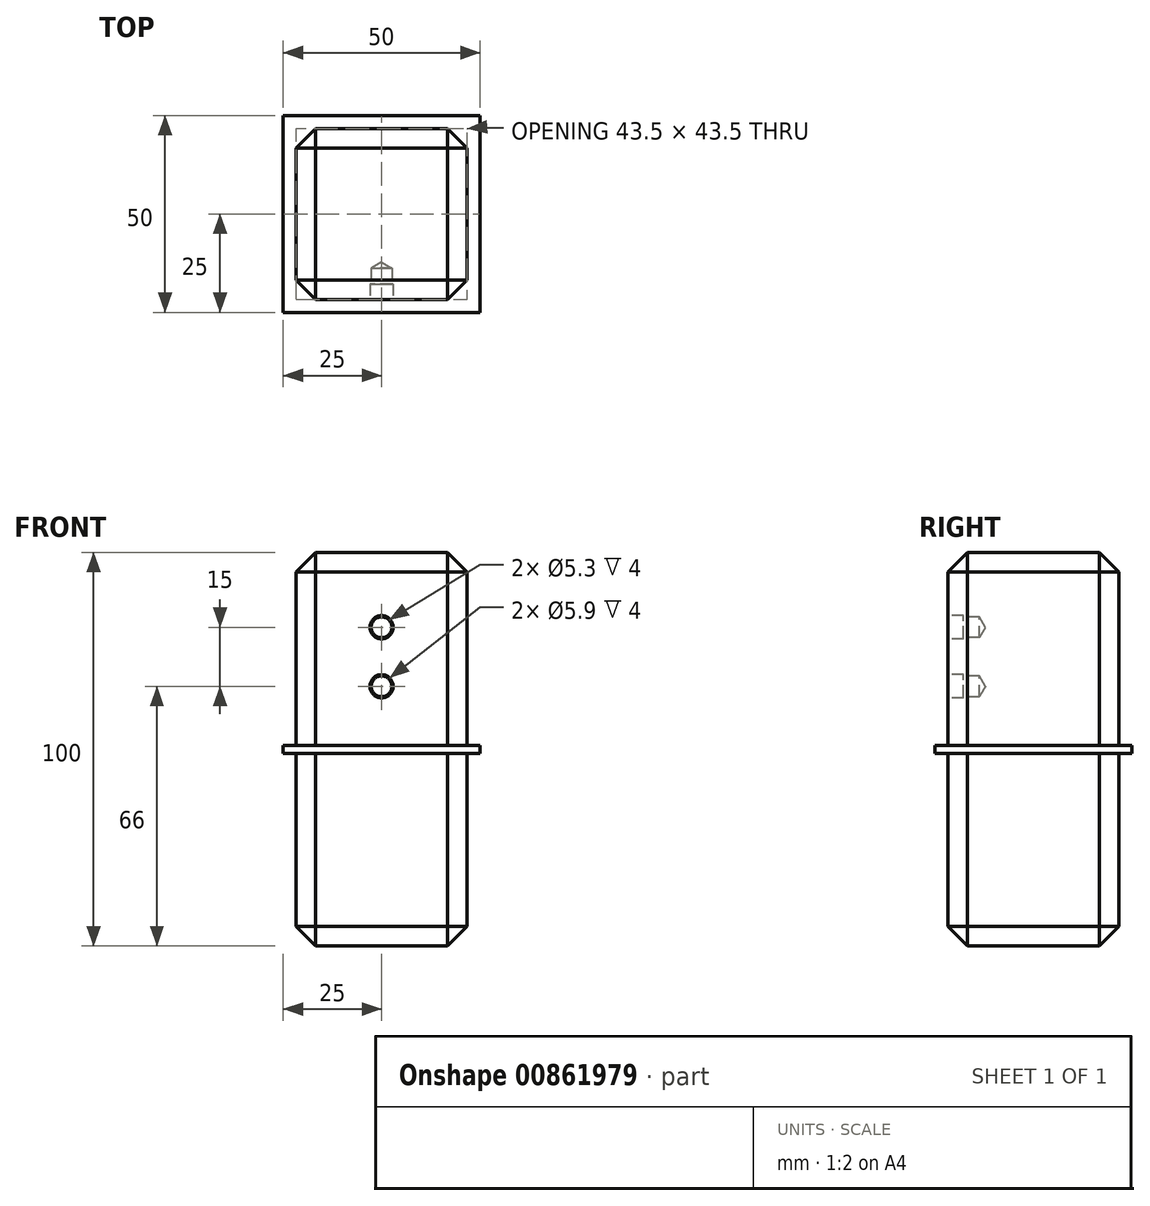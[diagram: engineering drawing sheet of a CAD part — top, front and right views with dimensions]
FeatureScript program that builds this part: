
annotation { "Feature Type Name" : "Feature", "Feature Type Description" : "" }
export const myFeature = defineFeature(function(context is Context, id is Id, definition is map)
    precondition{}
    {
        {
            var Q0;
            Q0=qCreatedBy(makeId("Top.planeOp"),FACE);
            var sketch = newSketch(context, id + "F0", { "sketchPlane" : qUnion([Q0])});
            skLineSegment(sketch, "E0.bottom", {"start": v(-22.5, 22.5) * mm, "end": v(22.5, 22.5) * mm, "construction": true});
            skLineSegment(sketch, "E0.top", {"start": v(-22.5, -22.5) * mm, "end": v(22.5, -22.5) * mm, "construction": true});
            skLineSegment(sketch, "E0.left", {"start": v(-22.5, 22.5) * mm, "end": v(-22.5, -22.5) * mm, "construction": true});
            skLineSegment(sketch, "E0.right", {"start": v(22.5, 22.5) * mm, "end": v(22.5, -22.5) * mm, "construction": true});
            skPoint(sketch, "E0.middle", {"position": v(0, 0) * mm});
            skLineSegment(sketch, "E1.bottom", {"start": v(-21.75, 21.75) * mm, "end": v(21.75, 21.75) * mm});
            skLineSegment(sketch, "E1.top", {"start": v(-21.75, -21.75) * mm, "end": v(21.75, -21.75) * mm});
            skLineSegment(sketch, "E1.left", {"start": v(-21.75, 21.75) * mm, "end": v(-21.75, -21.75) * mm});
            skLineSegment(sketch, "E1.right", {"start": v(21.75, 21.75) * mm, "end": v(21.75, -21.75) * mm});
            skSolve(sketch);
        }
        {
            var Q0;
            Q0 = qSketchRegion(id + "F0", true);
            extrude(context, id + "F1", {"entities" : qUnion([Q0]), "depth" : 100 * mm, "offsetDistance" : 25 * mm, "symmetric" : true});
        }
        {
            var Q0;
            Q0=qCreatedBy(makeId("Top.planeOp"),FACE);
            var sketch = newSketch(context, id + "F2", { "sketchPlane" : qUnion([Q0])});
            skLineSegment(sketch, "E2.bottom", {"start": v(-25, 25) * mm, "end": v(25, 25) * mm});
            skLineSegment(sketch, "E2.top", {"start": v(-25, -25) * mm, "end": v(25, -25) * mm});
            skLineSegment(sketch, "E2.left", {"start": v(-25, 25) * mm, "end": v(-25, -25) * mm});
            skLineSegment(sketch, "E2.right", {"start": v(25, 25) * mm, "end": v(25, -25) * mm});
            skPoint(sketch, "E2.middle", {"position": v(0, 0) * mm});
            skSolve(sketch);
        }
        {
            var Q0;
            Q0 = qSketchRegion(id + "F2", true);
            extrude(context, id + "F3", {"entities" : qUnion([Q0]), "operationType" : NewBodyOperationType.ADD, "depth" : 2 * mm, "offsetDistance" : 25 * mm, "symmetric" : true});
        }
        {
            var Q0;
            Q0=makeQuery(id+"F1.opExtrude","CAP_FACE",FACE,{"disambiguationData":[OSD([sQuery(id+"F0.wireOp",EDGE,"E1.bottom"),sQuery(id+"F0.wireOp",EDGE,"E1.top"),sQuery(id+"F0.wireOp",EDGE,"E1.left"),sQuery(id+"F0.wireOp",EDGE,"E1.right")])],"isStart":false});
            var Q1;
            {var subQ0=sQuery(id+"F0.wireOp",EDGE,"E1.bottom");var subQ1=sQuery(id+"F0.wireOp",EDGE,"E1.left");Q1=makeQuery(id+"F3.boolean.opBoolean","SPLIT",EDGE,{"disambiguationData":[TD([makeQuery(id+"F1.opExtrude","CAP_FACE",FACE,{"disambiguationData":[OSD([subQ0,sQuery(id+"F0.wireOp",EDGE,"E1.top"),subQ1,sQuery(id+"F0.wireOp",EDGE,"E1.right")])],"isStart":false})])],"derivedFrom":makeQuery(id+"F1.opExtrude","SWEPT_EDGE",EDGE,{"disambiguationData":[OSD([subQ0,subQ1])]})});}
            var Q2;
            {var subQ0=sQuery(id+"F0.wireOp",EDGE,"E1.left");var subQ1=sQuery(id+"F0.wireOp",EDGE,"E1.top");Q2=makeQuery(id+"F3.boolean.opBoolean","SPLIT",EDGE,{"disambiguationData":[TD([makeQuery(id+"F1.opExtrude","CAP_FACE",FACE,{"disambiguationData":[OSD([sQuery(id+"F0.wireOp",EDGE,"E1.bottom"),subQ1,subQ0,sQuery(id+"F0.wireOp",EDGE,"E1.right")])],"isStart":false})])],"derivedFrom":makeQuery(id+"F1.opExtrude","SWEPT_EDGE",EDGE,{"disambiguationData":[OSD([subQ1,subQ0])]})});}
            var Q3;
            {var subQ0=sQuery(id+"F0.wireOp",EDGE,"E1.bottom");var subQ1=sQuery(id+"F0.wireOp",EDGE,"E1.right");Q3=makeQuery(id+"F3.boolean.opBoolean","SPLIT",EDGE,{"disambiguationData":[TD([makeQuery(id+"F1.opExtrude","CAP_FACE",FACE,{"disambiguationData":[OSD([subQ0,sQuery(id+"F0.wireOp",EDGE,"E1.top"),sQuery(id+"F0.wireOp",EDGE,"E1.left"),subQ1])],"isStart":false})])],"derivedFrom":makeQuery(id+"F1.opExtrude","SWEPT_EDGE",EDGE,{"disambiguationData":[OSD([subQ0,subQ1])]})});}
            var Q4;
            {var subQ0=sQuery(id+"F0.wireOp",EDGE,"E1.right");var subQ1=sQuery(id+"F0.wireOp",EDGE,"E1.top");Q4=makeQuery(id+"F3.boolean.opBoolean","SPLIT",EDGE,{"disambiguationData":[TD([makeQuery(id+"F1.opExtrude","CAP_FACE",FACE,{"disambiguationData":[OSD([sQuery(id+"F0.wireOp",EDGE,"E1.bottom"),subQ1,sQuery(id+"F0.wireOp",EDGE,"E1.left"),subQ0])],"isStart":false})])],"derivedFrom":makeQuery(id+"F1.opExtrude","SWEPT_EDGE",EDGE,{"disambiguationData":[OSD([subQ1,subQ0])]})});}
            var Q5;
            {var subQ0=sQuery(id+"F0.wireOp",EDGE,"E1.left");var subQ1=sQuery(id+"F0.wireOp",EDGE,"E1.top");Q5=makeQuery(id+"F3.boolean.opBoolean","SPLIT",EDGE,{"disambiguationData":[TD([makeQuery(id+"F1.opExtrude","CAP_FACE",FACE,{"disambiguationData":[OSD([sQuery(id+"F0.wireOp",EDGE,"E1.bottom"),subQ1,subQ0,sQuery(id+"F0.wireOp",EDGE,"E1.right")])],"isStart":true})])],"derivedFrom":makeQuery(id+"F1.opExtrude","SWEPT_EDGE",EDGE,{"disambiguationData":[OSD([subQ1,subQ0])]})});}
            var Q6;
            {var subQ0=sQuery(id+"F0.wireOp",EDGE,"E1.right");var subQ1=sQuery(id+"F0.wireOp",EDGE,"E1.top");Q6=makeQuery(id+"F3.boolean.opBoolean","SPLIT",EDGE,{"disambiguationData":[TD([makeQuery(id+"F1.opExtrude","CAP_FACE",FACE,{"disambiguationData":[OSD([sQuery(id+"F0.wireOp",EDGE,"E1.bottom"),subQ1,sQuery(id+"F0.wireOp",EDGE,"E1.left"),subQ0])],"isStart":true})])],"derivedFrom":makeQuery(id+"F1.opExtrude","SWEPT_EDGE",EDGE,{"disambiguationData":[OSD([subQ1,subQ0])]})});}
            var Q7;
            {var subQ0=sQuery(id+"F0.wireOp",EDGE,"E1.bottom");var subQ1=sQuery(id+"F0.wireOp",EDGE,"E1.right");Q7=makeQuery(id+"F3.boolean.opBoolean","SPLIT",EDGE,{"disambiguationData":[TD([makeQuery(id+"F1.opExtrude","CAP_FACE",FACE,{"disambiguationData":[OSD([subQ0,sQuery(id+"F0.wireOp",EDGE,"E1.top"),sQuery(id+"F0.wireOp",EDGE,"E1.left"),subQ1])],"isStart":true})])],"derivedFrom":makeQuery(id+"F1.opExtrude","SWEPT_EDGE",EDGE,{"disambiguationData":[OSD([subQ0,subQ1])]})});}
            var Q8;
            {var subQ0=sQuery(id+"F0.wireOp",EDGE,"E1.bottom");var subQ1=sQuery(id+"F0.wireOp",EDGE,"E1.left");Q8=makeQuery(id+"F3.boolean.opBoolean","SPLIT",EDGE,{"disambiguationData":[TD([makeQuery(id+"F1.opExtrude","CAP_FACE",FACE,{"disambiguationData":[OSD([subQ0,sQuery(id+"F0.wireOp",EDGE,"E1.top"),subQ1,sQuery(id+"F0.wireOp",EDGE,"E1.right")])],"isStart":true})])],"derivedFrom":makeQuery(id+"F1.opExtrude","SWEPT_EDGE",EDGE,{"disambiguationData":[OSD([subQ0,subQ1])]})});}
            var Q9;
            Q9=makeQuery(id+"F1.opExtrude","CAP_FACE",FACE,{"disambiguationData":[OSD([sQuery(id+"F0.wireOp",EDGE,"E1.bottom"),sQuery(id+"F0.wireOp",EDGE,"E1.top"),sQuery(id+"F0.wireOp",EDGE,"E1.left"),sQuery(id+"F0.wireOp",EDGE,"E1.right")])],"isStart":true});
            chamfer(context, id + "F4", {"entities" : qUnion([Q0, Q1, Q2, Q3, Q4, Q5, Q6, Q7, Q8, Q9]), "width" : 5 * mm, "tangentPropagation" : true});
        }
        {
            var Q0;
            {var subQ0=sQuery(id+"F0.wireOp",EDGE,"E1.right");var subQ1=sQuery(id+"F0.wireOp",EDGE,"E1.left");var subQ2=sQuery(id+"F0.wireOp",EDGE,"E1.top");Q0=makeQuery(id+"F3.boolean.opBoolean","SPLIT",FACE,{"disambiguationData":[TD([makeQuery(id+"F1.opExtrude","CAP_FACE",FACE,{"disambiguationData":[OSD([sQuery(id+"F0.wireOp",EDGE,"E1.bottom"),subQ2,subQ1,subQ0])],"isStart":false})])],"derivedFrom":makeQuery(id+"F1.opExtrude","SWEPT_FACE",FACE,{"disambiguationData":[OSD([subQ2])]})});}
            var sketch = newSketch(context, id + "F5", { "sketchPlane" : qUnion([Q0])});
            skLineSegment(sketch, "E3", {"start": v(0, 45) * mm, "end": v(0, 0) * mm, "construction": true});
            skPoint(sketch, "E4", {"position": v(0, 31) * mm});
            skPoint(sketch, "E5", {"position": v(0, 16) * mm});
            skSolve(sketch);
        }
        {
            var Q0;
            Q0=sQuery(id+"F5.wireOp",VERTEX,"E5");
            var Q1;
            Q1=sQuery(id+"F5.wireOp",VERTEX,"E4");
            var Q2;
            Q2=makeQuery(id+"F1.opExtrude","SWEPT_BODY",BODY,{"disambiguationData":[OSD([sQuery(id+"F0.wireOp",EDGE,"E1.bottom"),sQuery(id+"F0.wireOp",EDGE,"E1.top"),sQuery(id+"F0.wireOp",EDGE,"E1.left"),sQuery(id+"F0.wireOp",EDGE,"E1.right")])]});
            hole(context, id + "F6", {"style" : HoleStyle.C_BORE, "endStyle" : HoleEndStyle.BLIND, "standardTappedOrClearance" : lookupTablePath({ "standard" : "ISO", "size" : "5.3", "type" : "Drilled" }), "standardBlindInLast" : lookupTablePath({ "standard" : "ISO", "size" : "5.3", "type" : "Drilled" }), "holeDiameter" : 5.3 * mm, "cBoreDiameter" : 5.9 * mm, "cBoreDepth" : 4 * mm, "majorDiameter" : 5 * mm, "holeDepth" : 8 * mm, "isTappedThrough" : true, "tappedDepth" : 12 * mm, "tapClearance" : 3, "locations" : qUnion([Q0, Q1]), "scope" : qUnion([Q2])});
        }
        {
            var Q0;
            Q0=qCreatedBy(makeId("Right.planeOp"),FACE);
            var sketch = newSketch(context, id + "F7", { "sketchPlane" : qUnion([Q0])});
            skLineSegment(sketch, "E6", {"start": v(0, 0) * mm, "end": v(0, 50) * mm});
            skSolve(sketch);
        }
    });
